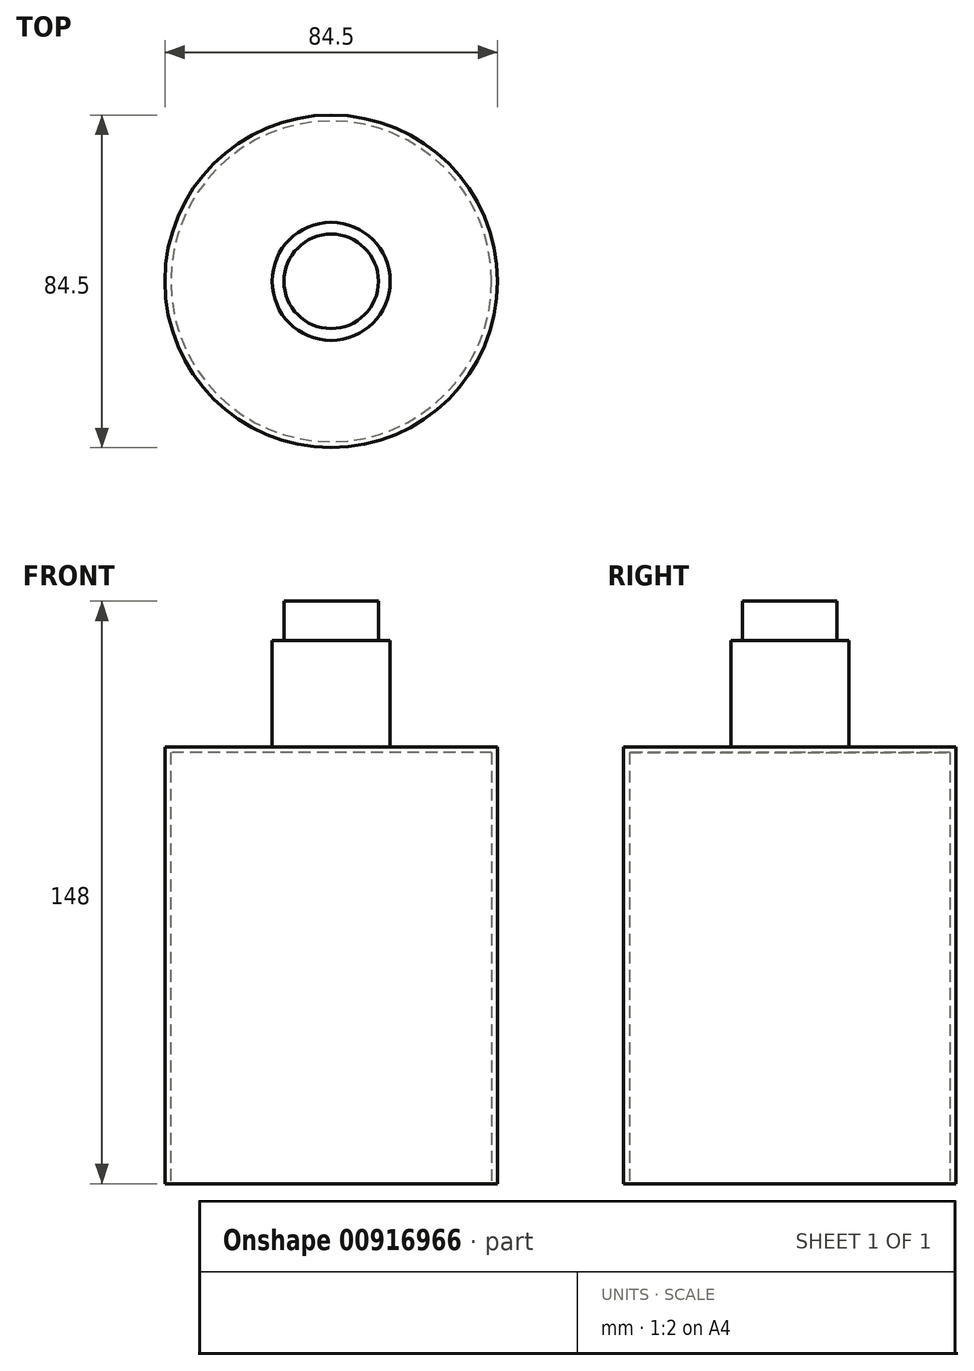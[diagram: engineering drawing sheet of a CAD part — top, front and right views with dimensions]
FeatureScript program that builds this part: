
annotation { "Feature Type Name" : "Feature", "Feature Type Description" : "" }
export const myFeature = defineFeature(function(context is Context, id is Id, definition is map)
    precondition{}
    {
        {
            var Q0;
            Q0=qCreatedBy(makeId("Top.planeOp"),FACE);
            var sketch = newSketch(context, id + "F0", { "sketchPlane" : qUnion([Q0])});
            skCircle(sketch, "E0", {"center": v(0, 0) * mm, "radius": 42.25 * mm});
            skSolve(sketch);
        }
        {
            var Q0;
            Q0=makeQuery(id+"F0.imprint","IMPRINT",FACE,{"disambiguationData":[TD([[makeQuery(id+"F0.imprint","IMPRINT",EDGE,{"derivedFrom":sQuery(id+"F0.wireOp",EDGE,"E0")}),1.0]])]});
            extrude(context, id + "F1", {"entities" : qUnion([Q0]), "depth" : 111 * mm, "offsetDistance" : 25 * mm});
        }
        {
            var Q0;
            Q0=makeQuery(id+"F1.opExtrude","CAP_FACE",FACE,{"disambiguationData":[OSD([sQuery(id+"F0.wireOp",EDGE,"E0")])],"isStart":true});
            shell(context, id + "F2", {"entities" : qUnion([Q0]), "thickness" : 1.5 * mm});
        }
        {
            var Q0;
            Q0=makeQuery(id+"F1.opExtrude","CAP_FACE",FACE,{"disambiguationData":[OSD([sQuery(id+"F0.wireOp",EDGE,"E0")])],"isStart":false});
            var sketch = newSketch(context, id + "F3", { "sketchPlane" : qUnion([Q0])});
            skCircle(sketch, "E1", {"center": v(0, 0) * mm, "radius": 15 * mm});
            skSolve(sketch);
        }
        {
            var Q0;
            Q0 = qSketchRegion(id + "F3", true);
            extrude(context, id + "F4", {"entities" : qUnion([Q0]), "operationType" : NewBodyOperationType.ADD, "depth" : 27 * mm, "offsetDistance" : 25 * mm});
        }
        {
            var Q0;
            Q0=makeQuery(id+"F4.opExtrude","CAP_FACE",FACE,{"disambiguationData":[OSD([sQuery(id+"F3.wireOp",EDGE,"E1")])],"isStart":false});
            var sketch = newSketch(context, id + "F5", { "sketchPlane" : qUnion([Q0])});
            skCircle(sketch, "E2", {"center": v(0, 0) * mm, "radius": 12 * mm});
            skSolve(sketch);
        }
        {
            var Q0;
            Q0=makeQuery(id+"F5.imprint","IMPRINT",FACE,{"disambiguationData":[TD([[makeQuery(id+"F5.imprint","IMPRINT",EDGE,{"derivedFrom":sQuery(id+"F5.wireOp",EDGE,"E2")}),1.0]])]});
            extrude(context, id + "F6", {"entities" : qUnion([Q0]), "operationType" : NewBodyOperationType.ADD, "depth" : 10 * mm, "offsetDistance" : 25 * mm});
        }
    });
